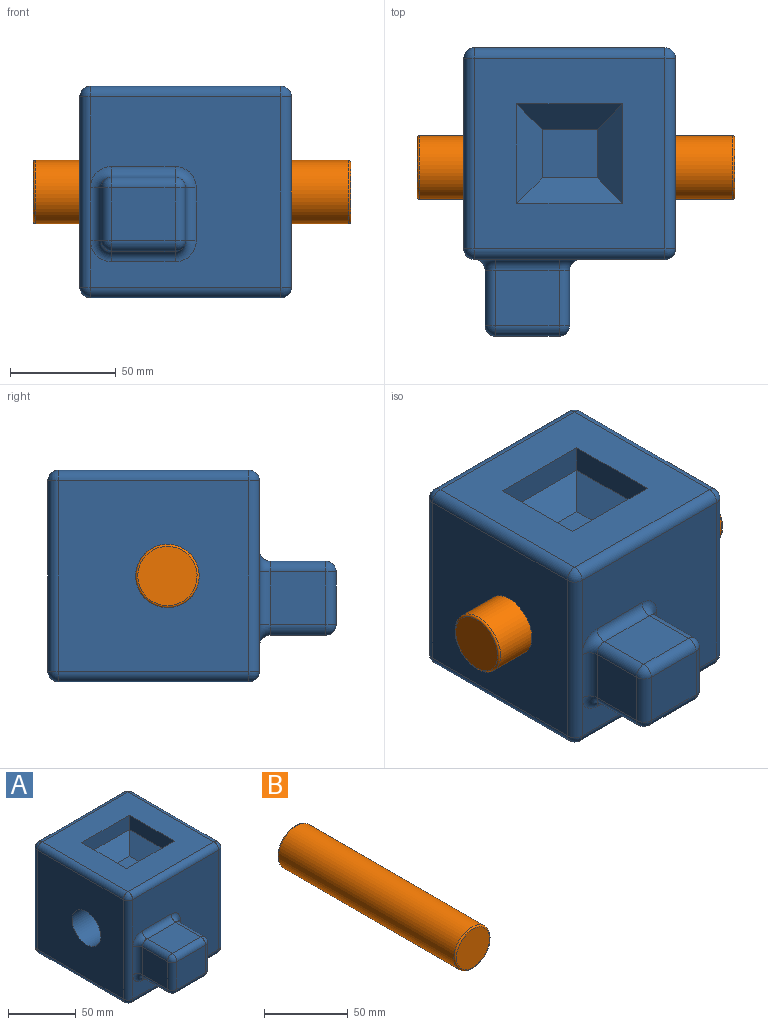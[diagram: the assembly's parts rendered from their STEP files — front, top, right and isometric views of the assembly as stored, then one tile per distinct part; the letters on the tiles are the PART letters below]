
ASSEMBLY  parts=2 mates=1
PART A: 62 faces, bbox 100x136.2x100 mm
  f0: plane 90x90mm, normal (0,0,1), area 5750mm2, adj f21,f22,f32,f33,f53,f54,f55,f56
  f1: plane 90x90mm, normal (-1,0,0), area 7393.1mm2, adj f20,f31,f32,f40,f51
  f2: plane 90x90mm, normal (0,0,-1), area 8100mm2, adj f18,f19,f30,f31
  f3: plane 90x90mm, normal (1,0,0), area 7295.8mm2, adj f15,f18,f22,f23,f52
  f4: plane 90x90mm, normal (0,-1,0), area 5935.8mm2, adj f23,f28,f29,f30,f33,f34,f35,f38
  f5: plane 90x90mm, normal (0,1,0), area 8100mm2, adj f15,f19,f20,f21
  f6: plane 30x26.22mm, normal (0,0,-1), area 786.7mm2, adj f7,f13,f35,f46
  f7: cylinder r=5mm len=26.22mm, axis (0,1,0), area 206mm2, adj f6,f8,f29,f44
  f8: plane 26.22x25mm, normal (1,0,0), area 655.6mm2, adj f7,f9,f28,f43
  f9: cylinder r=5mm len=26.22mm, axis (0,1,0), area 206mm2, adj f8,f10,f34,f45
  f10: plane 30x26.22mm, normal (0,0,1), area 786.7mm2, adj f9,f11,f38,f47
  f11: cylinder r=5mm len=26.22mm, axis (0,1,0), area 206mm2, adj f10,f12,f41,f49
  f12: plane 26.22x25mm, normal (-1,0,0), area 655.6mm2, adj f11,f13,f42,f50
  f13: cylinder r=5mm len=26.22mm, axis (0,1,0), area 206mm2, adj f6,f12,f39,f48
  f14: plane 30x25mm, normal (0,-1,0), area 750mm2, adj f43,f46,f47,f50
  f15: cylinder r=5mm len=90mm, axis (0,0,1), area 706.9mm2, adj f3,f5,f16,f17
  f16: sphere r=5mm, area 39.3mm2, adj f15,f18,f19
  f17: sphere r=5mm, area 39.3mm2, adj f15,f21,f22
  f18: cylinder r=5mm len=90mm, axis (0,1,0), area 706.9mm2, adj f2,f3,f16,f24
  f19: cylinder r=5mm len=90mm, axis (1,0,0), area 706.9mm2, adj f2,f5,f16,f25
  f20: cylinder r=5mm len=90mm, axis (0,0,-1), area 706.9mm2, adj f1,f5,f25,f26
  f21: cylinder r=5mm len=90mm, axis (-1,0,0), area 706.9mm2, adj f0,f5,f17,f26
  f22: cylinder r=5mm len=90mm, axis (0,-1,0), area 706.9mm2, adj f0,f3,f17,f27
  f23: cylinder r=5mm len=90mm, axis (0,0,-1), area 706.9mm2, adj f3,f4,f24,f27
  f24: sphere r=5mm, area 39.3mm2, adj f18,f23,f30
  f25: sphere r=5mm, area 39.3mm2, adj f19,f20,f31
  f26: sphere r=5mm, area 39.3mm2, adj f20,f21,f32
  f27: sphere r=5mm, area 39.3mm2, adj f22,f23,f33
  f28: cylinder r=5mm len=25mm, axis (0,0,1), area 196.3mm2, adj f4,f8,f29,f34
  f29: torus R=10mm, axis (0,-1,0), area 84.1mm2, adj f4,f7,f28,f35
  f30: cylinder r=5mm len=90mm, axis (-1,0,0), area 706.9mm2, adj f2,f4,f24,f36
  f31: cylinder r=5mm len=90mm, axis (0,-1,0), area 706.9mm2, adj f1,f2,f25,f36
  f32: cylinder r=5mm len=90mm, axis (0,1,0), area 706.9mm2, adj f0,f1,f26,f37
  f33: cylinder r=5mm len=90mm, axis (1,0,0), area 706.9mm2, adj f0,f4,f27,f37
  f34: torus R=10mm, axis (0,-1,0), area 84.1mm2, adj f4,f9,f28,f38
  f35: cylinder r=5mm len=30mm, axis (1,0,0), area 235.6mm2, adj f4,f6,f29,f39
  f36: sphere r=5mm, area 39.3mm2, adj f30,f31,f40
  f37: sphere r=5mm, area 39.3mm2, adj f32,f33,f40
  f38: cylinder r=5mm len=30mm, axis (-1,0,0), area 235.6mm2, adj f4,f10,f34,f41
  f39: torus R=10mm, axis (0,-1,0), area 84.1mm2, adj f4,f13,f35,f42
  f40: cylinder r=5mm len=90mm, axis (0,0,1), area 706.9mm2, adj f1,f4,f36,f37,f42
  f41: torus R=10mm, axis (0,-1,0), area 84.1mm2, adj f4,f11,f38,f42
  f42: cylinder r=5mm len=25mm, axis (0,0,-1), area 196.3mm2, adj f12,f39,f40,f41
  f43: cylinder r=5mm len=25mm, axis (0,0,-1), area 196.3mm2, adj f8,f14,f44,f45
  f44: sphere r=5mm, area 39.3mm2, adj f7,f43,f46
  f45: sphere r=5mm, area 39.3mm2, adj f9,f43,f47
  f46: cylinder r=5mm len=30mm, axis (-1,0,0), area 235.6mm2, adj f6,f14,f44,f48
  f47: cylinder r=5mm len=30mm, axis (1,0,0), area 235.6mm2, adj f10,f14,f45,f49
  f48: sphere r=5mm, area 39.3mm2, adj f13,f46,f50
  f49: sphere r=5mm, area 39.3mm2, adj f11,f47,f50
  f50: cylinder r=5mm len=25mm, axis (0,0,1), area 196.3mm2, adj f12,f14,f48,f49
  f51: cylinder r=15mm len=99mm, axis (1,0,0), area 9330.5mm2, adj f1,f52
  f52: torus R=16mm, axis (-1,0,0), area 151.6mm2, adj f3,f51
  f53: plane 47x13mm, normal (1,0,0), area 611mm2, adj f0,f54,f56,f58
  f54: plane 50x13mm, normal (0,1,0), area 650mm2, adj f0,f53,f55,f59
  f55: plane 47x13mm, normal (-1,0,0), area 611mm2, adj f0,f54,f56,f61
  f56: plane 50x13mm, normal (0,-1,0), area 650mm2, adj f0,f53,f55,f60
  f57: plane 26x23mm, normal (0,0,1), area 598mm2, adj f58,f59,f60,f61
  f58: plane 47x12mm, normal (0.71,0,0.71), area 594mm2, adj f53,f57,f59,f60
  f59: plane 50x12mm, normal (0,0.71,0.71), area 644.9mm2, adj f54,f57,f58,f61
  f60: plane 50x12mm, normal (0,-0.71,0.71), area 644.9mm2, adj f56,f57,f58,f61
  f61: plane 47x12mm, normal (-0.71,0,0.71), area 594mm2, adj f55,f57,f59,f60
PART B: 5 faces, bbox 32.5x150x32.5 mm
  f0: cylinder r=15mm len=148mm, axis (0,1,0), area 13948.7mm2, adj f3,f4
  f1: plane 28x28mm, normal (0,-1,0), area 615.8mm2, adj f4
  f2: plane 28x28mm, normal (0,1,0), area 615.8mm2, adj f3
  f3: torus R=14mm, axis (0,-1,0), area 144.5mm2, adj f0,f2
  f4: torus R=14mm, axis (0,-1,0), area 144.5mm2, adj f0,f1
PLACE A t=(-14.71,2.87,11.55)mm fixed
PLACE B rot(axis=(0.46,0.46,-0.76),105.5deg) t=(-11.71,-3.63,11.55)mm
MATE cylindrical B.f0 <-> A.f52  axis (1,0,0) through (-11.71,-3.63,11.55)mm
